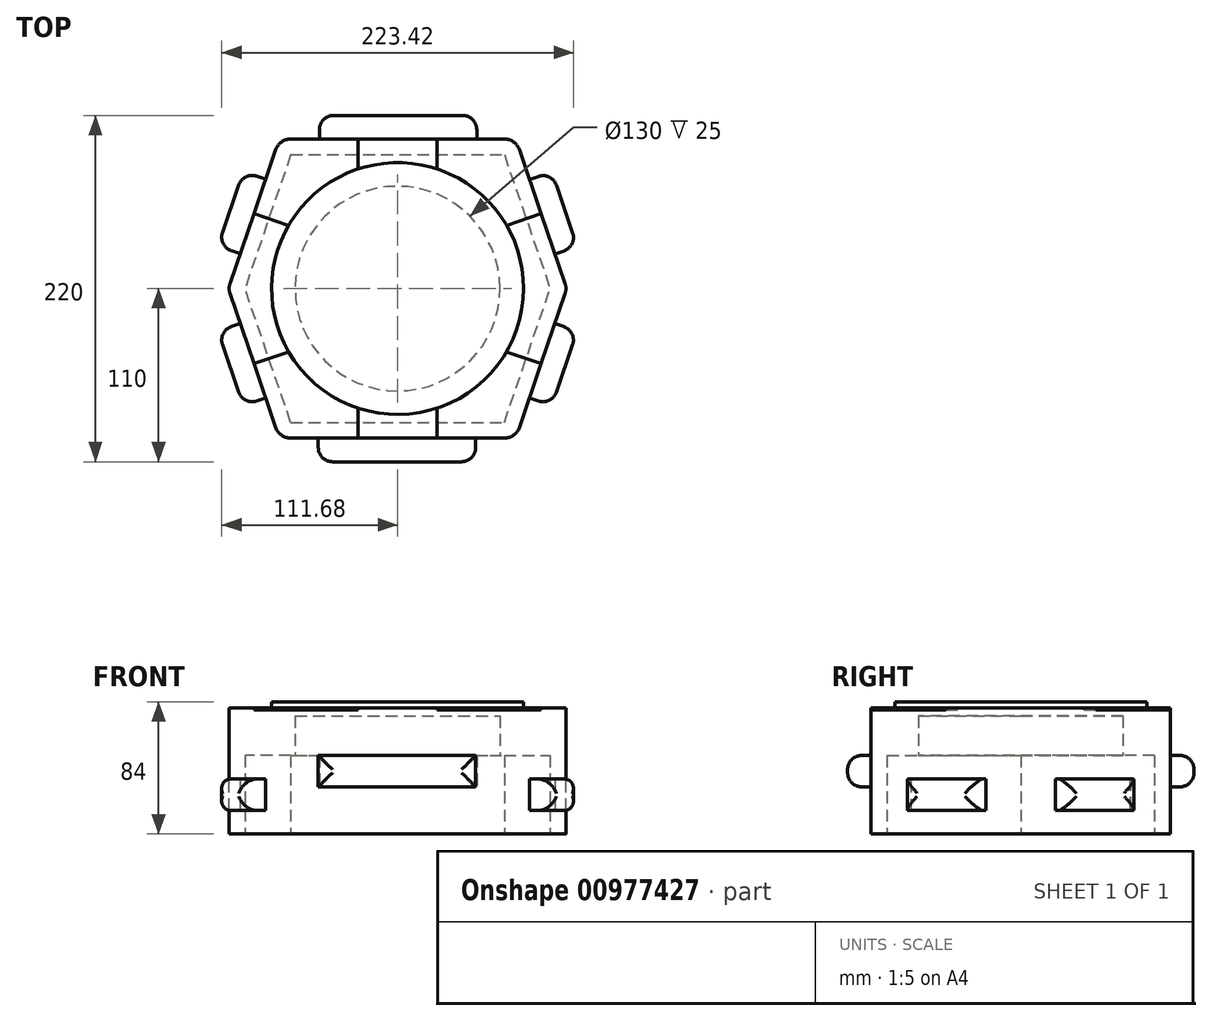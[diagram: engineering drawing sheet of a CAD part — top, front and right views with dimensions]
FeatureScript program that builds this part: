
annotation { "Feature Type Name" : "Feature", "Feature Type Description" : "" }
export const myFeature = defineFeature(function(context is Context, id is Id, definition is map)
    precondition{}
    {
        {
            var Q0;
            Q0=qCreatedBy(makeId("Top.planeOp"),FACE);
            var sketch = newSketch(context, id + "F0", { "sketchPlane" : qUnion([Q0])});
            skLineSegment(sketch, "E0", {"start": v(0, 95) * mm, "end": v(0, -95) * mm});
            skLineSegment(sketch, "E1", {"start": v(107.5, 0) * mm, "end": v(-107.5, 0) * mm});
            skLineSegment(sketch, "E2", {"start": v(-75, 95) * mm, "end": v(75, 95) * mm});
            skLineSegment(sketch, "E3", {"start": v(-75, -95) * mm, "end": v(75, -95) * mm});
            skLineSegment(sketch, "E4", {"start": v(-75, 95) * mm, "end": v(-107.5, 0) * mm});
            skLineSegment(sketch, "E5", {"start": v(-75, -95) * mm, "end": v(-107.5, 0) * mm});
            skLineSegment(sketch, "E6", {"start": v(75, 95) * mm, "end": v(107.5, 0) * mm});
            skLineSegment(sketch, "E7", {"start": v(75, -95) * mm, "end": v(107.5, 0) * mm});
            skSolve(sketch);
        }
        {
            var Q0;
            Q0=qSketchRegion(id+"F0",true);
            extrude(context, id + "F1", {"entities" : qUnion([Q0]), "depth" : 80 * mm, "offsetDistance" : 25 * mm});
        }
        {
            var Q0;
            Q0=makeQuery(id+"F1.opExtrude","CAP_FACE",FACE,{"disambiguationData":[OSD([sQuery(id+"F0.wireOp",EDGE,"E2"),sQuery(id+"F0.wireOp",EDGE,"E3"),sQuery(id+"F0.wireOp",EDGE,"E4"),sQuery(id+"F0.wireOp",EDGE,"E5"),sQuery(id+"F0.wireOp",EDGE,"E6"),sQuery(id+"F0.wireOp",EDGE,"E7")])],"isStart":false});
            var sketch = newSketch(context, id + "F2", { "sketchPlane" : qUnion([Q0])});
            skLineSegment(sketch, "E8", {"start": v(0, 60) * mm, "end": v(0, -60) * mm, "construction": true});
            skArc(sketch, "E9", {"start": v(0, -60) * mm, "mid": v(60, 0) * mm, "end": v(0, 60) * mm});
            skArc(sketch, "E10", {"start": v(0, -50) * mm, "mid": v(50, 0) * mm, "end": v(0, 50) * mm});
            skSolve(sketch);
        }
        {
            var Q0;
            Q0=makeQuery(id+"F2.imprint","IMPRINT",FACE,{"disambiguationData":[TD([[makeQuery(id+"F2.imprint","IMPRINT",EDGE,{"derivedFrom":sQuery(id+"F2.wireOp",EDGE,"E9")}),-1.0]])]});
            var Q1;
            Q1=sQuery(id+"F2.wireOp",EDGE,"E9");
            var Q2;
            Q2=sQuery(id+"F2.wireOp",EDGE,"E10");
            var Q3;
            Q3=sQuery(id+"F2.wireOp",EDGE,"E8");
            revolve(context, id + "F3", {"bodyType" : ToolBodyType.SURFACE, "surfaceOperationType" : NewSurfaceOperationType.NEW, "entities" : qUnion([Q0]), "surfaceEntities" : qUnion([Q1, Q2]), "axis" : qUnion([Q3]), "revolveType" : RevolveType.ONE_DIRECTION, "angle" : 180 * degree});
        }
        {
            var Q0;
            Q0=makeQuery(id+"F1.opExtrude","CAP_FACE",FACE,{"disambiguationData":[OSD([sQuery(id+"F0.wireOp",EDGE,"E2"),sQuery(id+"F0.wireOp",EDGE,"E3"),sQuery(id+"F0.wireOp",EDGE,"E4"),sQuery(id+"F0.wireOp",EDGE,"E5"),sQuery(id+"F0.wireOp",EDGE,"E6"),sQuery(id+"F0.wireOp",EDGE,"E7")])],"isStart":false});
            var sketch = newSketch(context, id + "F4", { "sketchPlane" : qUnion([Q0])});
            skCircle(sketch, "E11", {"center": v(0, 0) * mm, "radius": 80 * mm});
            skSolve(sketch);
        }
        {
            var Q0;
            Q0=qSketchRegion(id+"F4",true);
            extrude(context, id + "F5", {"entities" : qUnion([Q0]), "operationType" : NewBodyOperationType.ADD, "depth" : 4 * mm, "offsetDistance" : 25 * mm});
        }
        {
            var Q0;
            Q0=makeQuery(id+"F1.opExtrude","CAP_FACE",FACE,{"disambiguationData":[OSD([sQuery(id+"F0.wireOp",EDGE,"E2"),sQuery(id+"F0.wireOp",EDGE,"E3"),sQuery(id+"F0.wireOp",EDGE,"E4"),sQuery(id+"F0.wireOp",EDGE,"E5"),sQuery(id+"F0.wireOp",EDGE,"E6"),sQuery(id+"F0.wireOp",EDGE,"E7")])],"isStart":true});
            var sketch = newSketch(context, id + "F6", { "sketchPlane" : qUnion([Q0])});
            skLineSegment(sketch, "E12.0", {"start": v(-67.85, 85) * mm, "end": v(67.85, 85) * mm});
            skLineSegment(sketch, "E12.1", {"start": v(-67.85, -85) * mm, "end": v(-96.93, 0) * mm});
            skLineSegment(sketch, "E12.2", {"start": v(-67.85, -85) * mm, "end": v(67.85, -85) * mm});
            skLineSegment(sketch, "E12.3", {"start": v(-67.85, 85) * mm, "end": v(-96.93, 0) * mm});
            skLineSegment(sketch, "E12.4", {"start": v(67.85, -85) * mm, "end": v(96.93, 0) * mm});
            skLineSegment(sketch, "E12.5", {"start": v(67.85, 85) * mm, "end": v(96.93, 0) * mm});
            skSolve(sketch);
        }
        {
            var Q0;
            Q0=qSketchRegion(id+"F6",true);
            extrude(context, id + "F7", {"entities" : qUnion([Q0]), "operationType" : NewBodyOperationType.REMOVE, "oppositeDirection" : true, "depth" : 50 * mm, "offsetDistance" : 25 * mm});
        }
        {
            var Q0;
            Q0=makeQuery(id+"F7.boolean.opBoolean","COPY",FACE,{"derivedFrom":makeQuery(id+"F7.opExtrude","CAP_FACE",FACE,{"disambiguationData":[OSD([sQuery(id+"F6.wireOp",EDGE,"E12.0"),sQuery(id+"F6.wireOp",EDGE,"E12.1"),sQuery(id+"F6.wireOp",EDGE,"E12.2"),sQuery(id+"F6.wireOp",EDGE,"E12.3"),sQuery(id+"F6.wireOp",EDGE,"E12.4"),sQuery(id+"F6.wireOp",EDGE,"E12.5")])],"isStart":false})});
            var sketch = newSketch(context, id + "F8", { "sketchPlane" : qUnion([Q0])});
            skCircle(sketch, "E13", {"center": v(0, 0) * mm, "radius": 65 * mm});
            skSolve(sketch);
        }
        {
            var Q0;
            Q0=makeQuery(id+"F8.imprint","IMPRINT",FACE,{"disambiguationData":[TD([[makeQuery(id+"F8.imprint","IMPRINT",EDGE,{"derivedFrom":sQuery(id+"F8.wireOp",EDGE,"E13")}),1.0]])]});
            extrude(context, id + "F9", {"entities" : qUnion([Q0]), "operationType" : NewBodyOperationType.REMOVE, "oppositeDirection" : true, "depth" : 25 * mm, "offsetDistance" : 25 * mm});
        }
        {
            var Q0;
            Q0=makeQuery(id+"F1.opExtrude","CAP_FACE",FACE,{"disambiguationData":[OSD([sQuery(id+"F0.wireOp",EDGE,"E2"),sQuery(id+"F0.wireOp",EDGE,"E3"),sQuery(id+"F0.wireOp",EDGE,"E4"),sQuery(id+"F0.wireOp",EDGE,"E5"),sQuery(id+"F0.wireOp",EDGE,"E6"),sQuery(id+"F0.wireOp",EDGE,"E7")])],"isStart":false});
            var sketch = newSketch(context, id + "F10", { "sketchPlane" : qUnion([Q0])});
            skLineSegment(sketch, "E14", {"start": v(75, -95) * mm, "end": v(91.18, -47.7) * mm});
            skLineSegment(sketch, "E15", {"start": v(91.18, -47.7) * mm, "end": v(69.19, -40.17) * mm});
            skLineSegment(sketch, "E16", {"start": v(75, -95) * mm, "end": v(25, -95) * mm});
            skLineSegment(sketch, "E17", {"start": v(25, -95) * mm, "end": v(25, -76) * mm});
            skArc(sketch, "E18", {"start": v(25, -76) * mm, "mid": v(50.16, -61.86) * mm, "end": v(69.19, -40.17) * mm});
            skLineSegment(sketch, "E19", {"start": v(75, 95) * mm, "end": v(25, 95) * mm});
            skLineSegment(sketch, "E20", {"start": v(25, 95) * mm, "end": v(25, 76) * mm});
            skLineSegment(sketch, "E21", {"start": v(75, 95) * mm, "end": v(91.18, 47.7) * mm});
            skLineSegment(sketch, "E22", {"start": v(91.18, 47.7) * mm, "end": v(69.19, 40.17) * mm});
            skArc(sketch, "E23", {"start": v(69.19, 40.17) * mm, "mid": v(50.16, 61.86) * mm, "end": v(25, 76) * mm});
            skLineSegment(sketch, "E24", {"start": v(-75, 95) * mm, "end": v(-91.18, 47.7) * mm});
            skLineSegment(sketch, "E25", {"start": v(-91.18, 47.7) * mm, "end": v(-69.19, 40.17) * mm});
            skLineSegment(sketch, "E26", {"start": v(-75, 95) * mm, "end": v(-25, 95) * mm});
            skLineSegment(sketch, "E27", {"start": v(-25, 95) * mm, "end": v(-25, 76) * mm});
            skArc(sketch, "E28", {"start": v(-25, 76) * mm, "mid": v(-50.16, 61.86) * mm, "end": v(-69.19, 40.17) * mm});
            skLineSegment(sketch, "E29", {"start": v(-69.19, -40.17) * mm, "end": v(-91.18, -47.7) * mm});
            skLineSegment(sketch, "E30", {"start": v(-91.18, -47.7) * mm, "end": v(-75, -95) * mm});
            skLineSegment(sketch, "E31", {"start": v(-75, -95) * mm, "end": v(-25, -95) * mm});
            skLineSegment(sketch, "E32", {"start": v(-25, -95) * mm, "end": v(-25, -76) * mm});
            skArc(sketch, "E33", {"start": v(-69.19, -40.17) * mm, "mid": v(-50.16, -61.86) * mm, "end": v(-25, -76) * mm});
            skSolve(sketch);
        }
        {
            var Q0;
            Q0=qSketchRegion(id+"F10",true);
            extrude(context, id + "F11", {"entities" : qUnion([Q0]), "operationType" : NewBodyOperationType.REMOVE, "oppositeDirection" : true, "depth" : 1 * mm, "offsetDistance" : 25 * mm});
        }
        {
            var Q0;
            Q0=makeQuery(id+"F1.opExtrude","SWEPT_FACE",FACE,{"disambiguationData":[OSD([sQuery(id+"F0.wireOp",EDGE,"E3")])]});
            var sketch = newSketch(context, id + "F12", { "sketchPlane" : qUnion([Q0])});
            skSolve(sketch);
        }
        {
            var Q0;
            Q0=makeQuery(id+"F1.opExtrude","SWEPT_EDGE",EDGE,{"disambiguationData":[OSD([sQuery(id+"F0.wireOp",EDGE,"E3"),sQuery(id+"F0.wireOp",EDGE,"E5")])]});
            var Q1;
            Q1=makeQuery(id+"F1.opExtrude","SWEPT_EDGE",EDGE,{"disambiguationData":[OSD([sQuery(id+"F0.wireOp",EDGE,"E3"),sQuery(id+"F0.wireOp",EDGE,"E7")])]});
            var Q2;
            Q2=makeQuery(id+"F1.opExtrude","SWEPT_EDGE",EDGE,{"disambiguationData":[OSD([sQuery(id+"F0.wireOp",EDGE,"E1"),sQuery(id+"F0.wireOp",EDGE,"E6"),sQuery(id+"F0.wireOp",EDGE,"E7")])]});
            var Q3;
            Q3=makeQuery(id+"F1.opExtrude","SWEPT_EDGE",EDGE,{"disambiguationData":[OSD([sQuery(id+"F0.wireOp",EDGE,"E2"),sQuery(id+"F0.wireOp",EDGE,"E6")])]});
            var Q4;
            Q4=makeQuery(id+"F1.opExtrude","SWEPT_EDGE",EDGE,{"disambiguationData":[OSD([sQuery(id+"F0.wireOp",EDGE,"E2"),sQuery(id+"F0.wireOp",EDGE,"E4")])]});
            var Q5;
            Q5=makeQuery(id+"F1.opExtrude","SWEPT_EDGE",EDGE,{"disambiguationData":[OSD([sQuery(id+"F0.wireOp",EDGE,"E1"),sQuery(id+"F0.wireOp",EDGE,"E4"),sQuery(id+"F0.wireOp",EDGE,"E5")])]});
            fillet(context, id + "F13", {"entities" : qUnion([Q0, Q1, Q2, Q3, Q4, Q5]), "radius" : 10 * mm, "tangentPropagation" : true, "allowEdgeOverflow" : false});
        }
        {
            var Q0;
            Q0=makeQuery(id+"F1.opExtrude","SWEPT_FACE",FACE,{"disambiguationData":[OSD([sQuery(id+"F0.wireOp",EDGE,"E5")])]});
            var sketch = newSketch(context, id + "F14", { "sketchPlane" : qUnion([Q0])});
            skLineSegment(sketch, "E34.bottom", {"start": v(-11.38, 15) * mm, "end": v(38.62, 15) * mm});
            skLineSegment(sketch, "E34.top", {"start": v(-11.38, 35) * mm, "end": v(38.62, 35) * mm});
            skLineSegment(sketch, "E34.left", {"start": v(-11.38, 15) * mm, "end": v(-11.38, 35) * mm});
            skLineSegment(sketch, "E34.right", {"start": v(38.62, 15) * mm, "end": v(38.62, 35) * mm});
            skPoint(sketch, "E34.middle", {"position": v(13.62, 25) * mm});
            skSolve(sketch);
        }
        {
            var Q0;
            Q0=makeQuery(id+"F1.opExtrude","SWEPT_FACE",FACE,{"disambiguationData":[OSD([sQuery(id+"F0.wireOp",EDGE,"E4")])]});
            var sketch = newSketch(context, id + "F15", { "sketchPlane" : qUnion([Q0])});
            skLineSegment(sketch, "E35.bottom", {"start": v(-38.62, 35) * mm, "end": v(11.38, 35) * mm});
            skLineSegment(sketch, "E35.top", {"start": v(-38.62, 15) * mm, "end": v(11.38, 15) * mm});
            skLineSegment(sketch, "E35.left", {"start": v(-38.62, 35) * mm, "end": v(-38.62, 15) * mm});
            skLineSegment(sketch, "E35.right", {"start": v(11.38, 35) * mm, "end": v(11.38, 15) * mm});
            skPoint(sketch, "E35.middle", {"position": v(-13.62, 25) * mm});
            skSolve(sketch);
        }
        {
            var Q0;
            Q0=makeQuery(id+"F15.imprint","IMPRINT",FACE,{"disambiguationData":[TD([[makeQuery(id+"F15.imprint","IMPRINT",EDGE,{"derivedFrom":sQuery(id+"F15.wireOp",EDGE,"E35.bottom")}),-1.0]])]});
            extrude(context, id + "F16", {"entities" : qUnion([Q0]), "depth" : 15 * mm, "offsetDistance" : 25 * mm});
        }
        {
            var Q0;
            Q0=makeQuery(id+"F14.imprint","IMPRINT",FACE,{"disambiguationData":[TD([[makeQuery(id+"F14.imprint","IMPRINT",EDGE,{"derivedFrom":sQuery(id+"F14.wireOp",EDGE,"E34.bottom")}),1.0]])]});
            extrude(context, id + "F17", {"entities" : qUnion([Q0]), "depth" : 15 * mm, "offsetDistance" : 25 * mm});
        }
        {
            var Q0;
            Q0=makeQuery(id+"F1.opExtrude","SWEPT_FACE",FACE,{"disambiguationData":[OSD([sQuery(id+"F0.wireOp",EDGE,"E6")])]});
            var sketch = newSketch(context, id + "F18", { "sketchPlane" : qUnion([Q0])});
            skLineSegment(sketch, "E36.bottom", {"start": v(-11.54, 35) * mm, "end": v(38.46, 35) * mm});
            skLineSegment(sketch, "E36.top", {"start": v(-11.54, 15) * mm, "end": v(38.46, 15) * mm});
            skLineSegment(sketch, "E36.left", {"start": v(-11.54, 35) * mm, "end": v(-11.54, 15) * mm});
            skLineSegment(sketch, "E36.right", {"start": v(38.46, 35) * mm, "end": v(38.46, 15) * mm});
            skPoint(sketch, "E36.middle", {"position": v(13.46, 25) * mm});
            skPoint(sketch, "E36.middle.positionSnap0", {"position": v(13.46, 50) * mm});
            skPoint(sketch, "E36.centerSnap0", {"position": v(13.46, 50) * mm});
            skSolve(sketch);
        }
        {
            var Q0;
            Q0=makeQuery(id+"F18.imprint","IMPRINT",FACE,{"disambiguationData":[TD([[makeQuery(id+"F18.imprint","IMPRINT",EDGE,{"derivedFrom":sQuery(id+"F18.wireOp",EDGE,"E36.bottom")}),-1.0]])]});
            extrude(context, id + "F19", {"entities" : qUnion([Q0]), "depth" : 15 * mm, "offsetDistance" : 25 * mm});
        }
        {
            var Q0;
            Q0=makeQuery(id+"F1.opExtrude","SWEPT_FACE",FACE,{"disambiguationData":[OSD([sQuery(id+"F0.wireOp",EDGE,"E7")])]});
            var sketch = newSketch(context, id + "F20", { "sketchPlane" : qUnion([Q0])});
            skLineSegment(sketch, "E37.bottom", {"start": v(-38.62, 35) * mm, "end": v(11.38, 35) * mm});
            skLineSegment(sketch, "E37.top", {"start": v(-38.62, 15) * mm, "end": v(11.38, 15) * mm});
            skLineSegment(sketch, "E37.left", {"start": v(-38.62, 35) * mm, "end": v(-38.62, 15) * mm});
            skLineSegment(sketch, "E37.right", {"start": v(11.38, 35) * mm, "end": v(11.38, 15) * mm});
            skPoint(sketch, "E37.middle", {"position": v(-13.62, 25) * mm});
            skSolve(sketch);
        }
        {
            var Q0;
            Q0=qSketchRegion(id+"F20",true);
            extrude(context, id + "F21", {"entities" : qUnion([Q0]), "depth" : 15 * mm, "offsetDistance" : 25 * mm});
        }
        {
            var Q0;
            Q0=makeQuery(id+"F1.opExtrude","SWEPT_FACE",FACE,{"disambiguationData":[OSD([sQuery(id+"F0.wireOp",EDGE,"E2")])]});
            var sketch = newSketch(context, id + "F22", { "sketchPlane" : qUnion([Q0])});
            skLineSegment(sketch, "E38.bottom", {"start": v(-50.35, 50) * mm, "end": v(49.65, 50) * mm});
            skLineSegment(sketch, "E38.top", {"start": v(-50.35, 30) * mm, "end": v(49.65, 30) * mm});
            skLineSegment(sketch, "E38.left", {"start": v(-50.35, 50) * mm, "end": v(-50.35, 30) * mm});
            skLineSegment(sketch, "E38.right", {"start": v(49.65, 50) * mm, "end": v(49.65, 30) * mm});
            skSolve(sketch);
        }
        {
            var Q0;
            Q0=qSketchRegion(id+"F22",true);
            extrude(context, id + "F23", {"entities" : qUnion([Q0]), "depth" : 15 * mm, "offsetDistance" : 25 * mm});
        }
        {
            var Q0;
            {var subQ2=sQuery(id+"F0.wireOp",EDGE,"E3");Q0=makeQuery(id+"F12.imprint","IMPRINT",FACE,{"disambiguationData":[TD([[makeQuery(id+"F12.imprint","IMPRINT",EDGE,{"derivedFrom":makeQuery(id+"F1.opExtrude","CAP_EDGE",EDGE,{"disambiguationData":[OSD([subQ2])],"isStart":true})}),1.0]])]});}
            var sketch = newSketch(context, id + "F24", { "sketchPlane" : qUnion([Q0])});
            skLineSegment(sketch, "E39.bottom", {"start": v(-50.35, 50) * mm, "end": v(49.65, 50) * mm});
            skLineSegment(sketch, "E39.top", {"start": v(-50.35, 30) * mm, "end": v(49.65, 30) * mm});
            skLineSegment(sketch, "E39.left", {"start": v(-50.35, 50) * mm, "end": v(-50.35, 30) * mm});
            skLineSegment(sketch, "E39.right", {"start": v(49.65, 50) * mm, "end": v(49.65, 30) * mm});
            skSolve(sketch);
        }
        {
            var Q0;
            Q0=qSketchRegion(id+"F24",true);
            extrude(context, id + "F25", {"entities" : qUnion([Q0]), "depth" : 15 * mm, "offsetDistance" : 25 * mm});
        }
        {
            var Q0;
            Q0=makeQuery(id+"F21.opExtrude","CAP_EDGE",EDGE,{"disambiguationData":[OSD([sQuery(id+"F20.wireOp",EDGE,"E37.bottom")])],"isStart":false});
            var Q1;
            Q1=makeQuery(id+"F21.opExtrude","CAP_EDGE",EDGE,{"disambiguationData":[OSD([sQuery(id+"F20.wireOp",EDGE,"E37.left")])],"isStart":false});
            var Q2;
            Q2=makeQuery(id+"F21.opExtrude","CAP_EDGE",EDGE,{"disambiguationData":[OSD([sQuery(id+"F20.wireOp",EDGE,"E37.top")])],"isStart":false});
            var Q3;
            Q3=makeQuery(id+"F21.opExtrude","CAP_EDGE",EDGE,{"disambiguationData":[OSD([sQuery(id+"F20.wireOp",EDGE,"E37.right")])],"isStart":false});
            var Q4;
            Q4=makeQuery(id+"F19.opExtrude","CAP_EDGE",EDGE,{"disambiguationData":[OSD([sQuery(id+"F18.wireOp",EDGE,"E36.bottom")])],"isStart":false});
            var Q5;
            Q5=makeQuery(id+"F19.opExtrude","CAP_EDGE",EDGE,{"disambiguationData":[OSD([sQuery(id+"F18.wireOp",EDGE,"E36.left")])],"isStart":false});
            var Q6;
            Q6=makeQuery(id+"F19.opExtrude","CAP_EDGE",EDGE,{"disambiguationData":[OSD([sQuery(id+"F18.wireOp",EDGE,"E36.top")])],"isStart":false});
            var Q7;
            Q7=makeQuery(id+"F19.opExtrude","CAP_EDGE",EDGE,{"disambiguationData":[OSD([sQuery(id+"F18.wireOp",EDGE,"E36.right")])],"isStart":false});
            var Q8;
            Q8=makeQuery(id+"F17.opExtrude","CAP_EDGE",EDGE,{"disambiguationData":[OSD([sQuery(id+"F14.wireOp",EDGE,"E34.top")])],"isStart":false});
            var Q9;
            Q9=makeQuery(id+"F17.opExtrude","CAP_EDGE",EDGE,{"disambiguationData":[OSD([sQuery(id+"F14.wireOp",EDGE,"E34.right")])],"isStart":false});
            var Q10;
            Q10=makeQuery(id+"F17.opExtrude","CAP_EDGE",EDGE,{"disambiguationData":[OSD([sQuery(id+"F14.wireOp",EDGE,"E34.bottom")])],"isStart":false});
            var Q11;
            Q11=makeQuery(id+"F17.opExtrude","CAP_EDGE",EDGE,{"disambiguationData":[OSD([sQuery(id+"F14.wireOp",EDGE,"E34.left")])],"isStart":false});
            var Q12;
            Q12=makeQuery(id+"F16.opExtrude","CAP_EDGE",EDGE,{"disambiguationData":[OSD([sQuery(id+"F15.wireOp",EDGE,"E35.right")])],"isStart":false});
            var Q13;
            Q13=makeQuery(id+"F16.opExtrude","CAP_EDGE",EDGE,{"disambiguationData":[OSD([sQuery(id+"F15.wireOp",EDGE,"E35.bottom")])],"isStart":false});
            var Q14;
            Q14=makeQuery(id+"F16.opExtrude","CAP_EDGE",EDGE,{"disambiguationData":[OSD([sQuery(id+"F15.wireOp",EDGE,"E35.left")])],"isStart":false});
            var Q15;
            Q15=makeQuery(id+"F16.opExtrude","CAP_EDGE",EDGE,{"disambiguationData":[OSD([sQuery(id+"F15.wireOp",EDGE,"E35.top")])],"isStart":false});
            var Q16;
            Q16=makeQuery(id+"F23.opExtrude","CAP_EDGE",EDGE,{"disambiguationData":[OSD([sQuery(id+"F22.wireOp",EDGE,"E38.bottom")])],"isStart":false});
            var Q17;
            Q17=makeQuery(id+"F23.opExtrude","CAP_EDGE",EDGE,{"disambiguationData":[OSD([sQuery(id+"F22.wireOp",EDGE,"E38.left")])],"isStart":false});
            var Q18;
            Q18=makeQuery(id+"F23.opExtrude","CAP_EDGE",EDGE,{"disambiguationData":[OSD([sQuery(id+"F22.wireOp",EDGE,"E38.top")])],"isStart":false});
            var Q19;
            Q19=makeQuery(id+"F23.opExtrude","CAP_EDGE",EDGE,{"disambiguationData":[OSD([sQuery(id+"F22.wireOp",EDGE,"E38.right")])],"isStart":false});
            var Q20;
            Q20=makeQuery(id+"F25.opExtrude","CAP_EDGE",EDGE,{"disambiguationData":[OSD([sQuery(id+"F24.wireOp",EDGE,"E39.top")])],"isStart":false});
            var Q21;
            Q21=makeQuery(id+"F25.opExtrude","CAP_EDGE",EDGE,{"disambiguationData":[OSD([sQuery(id+"F24.wireOp",EDGE,"E39.right")])],"isStart":false});
            var Q22;
            Q22=makeQuery(id+"F25.opExtrude","CAP_EDGE",EDGE,{"disambiguationData":[OSD([sQuery(id+"F24.wireOp",EDGE,"E39.bottom")])],"isStart":false});
            var Q23;
            Q23=makeQuery(id+"F25.opExtrude","CAP_EDGE",EDGE,{"disambiguationData":[OSD([sQuery(id+"F24.wireOp",EDGE,"E39.left")])],"isStart":false});
            fillet(context, id + "F26", {"entities" : qUnion([Q0, Q1, Q2, Q3, Q4, Q5, Q6, Q7, Q8, Q9, Q10, Q11, Q12, Q13, Q14, Q15, Q16, Q17, Q18, Q19, Q20, Q21, Q22, Q23]), "radius" : 9 * mm, "tangentPropagation" : true, "allowEdgeOverflow" : false});
        }
    });
